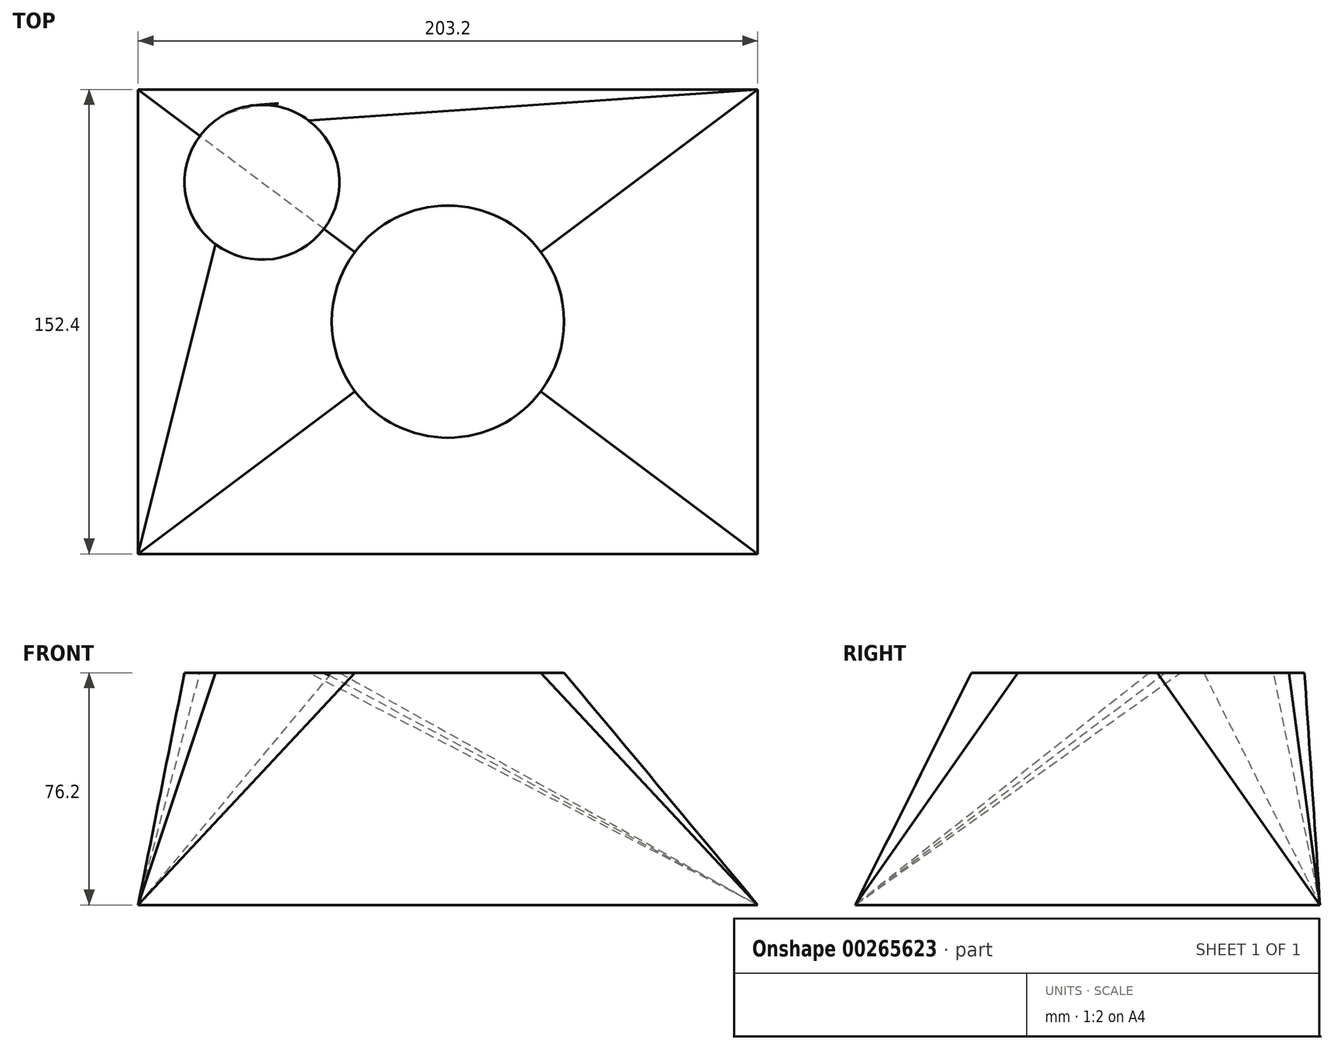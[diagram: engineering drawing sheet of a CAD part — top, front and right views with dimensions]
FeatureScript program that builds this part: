
annotation { "Feature Type Name" : "Feature", "Feature Type Description" : "" }
export const myFeature = defineFeature(function(context is Context, id is Id, definition is map)
    precondition{}
    {
        {
            var Q0;
            Q0=qCreatedBy(makeId("Top.planeOp"),FACE);
            cPlane(context, id + "F0", {"entities" : qUnion([Q0]), "cplaneType" : CPlaneType.OFFSET, "offset" : 76.2 * mm, "width" : 152.4 * mm, "height" : 152.4 * mm});
        }
        {
            var Q0;
            Q0=qCreatedBy(makeId("Top.planeOp"),FACE);
            var sketch = newSketch(context, id + "F1", { "sketchPlane" : qUnion([Q0])});
            skLineSegment(sketch, "E0.bottom", {"start": v(-101.6, 76.2) * mm, "end": v(101.6, 76.2) * mm});
            skLineSegment(sketch, "E0.top", {"start": v(-101.6, -76.2) * mm, "end": v(101.6, -76.2) * mm});
            skLineSegment(sketch, "E0.left", {"start": v(-101.6, 76.2) * mm, "end": v(-101.6, -76.2) * mm});
            skLineSegment(sketch, "E0.right", {"start": v(101.6, 76.2) * mm, "end": v(101.6, -76.2) * mm});
            skPoint(sketch, "E0.middle", {"position": v(0, 0) * mm});
            skSolve(sketch);
        }
        {
            var Q0;
            Q0=qCreatedBy(id+"F0.planeOp",FACE);
            var sketch = newSketch(context, id + "F2", { "sketchPlane" : qUnion([Q0])});
            skPoint(sketch, "E1.0", {"position": v(101.6, 76.2) * mm});
            skPoint(sketch, "E1.1", {"position": v(-101.6, 76.2) * mm});
            skPoint(sketch, "E1.2", {"position": v(101.6, -76.2) * mm});
            skPoint(sketch, "E1.3", {"position": v(-101.6, -76.2) * mm});
            skLineSegment(sketch, "E2", {"start": v(-101.6, 76.2) * mm, "end": v(-30.48, 22.86) * mm, "construction": true});
            skLineSegment(sketch, "E3", {"start": v(-101.6, -76.2) * mm, "end": v(30.48, 22.86) * mm, "construction": true});
            skLineSegment(sketch, "E4", {"start": v(-30.48, 22.86) * mm, "end": v(101.6, -76.2) * mm, "construction": true});
            skLineSegment(sketch, "E5", {"start": v(30.48, 22.86) * mm, "end": v(101.6, 76.2) * mm, "construction": true});
            skArc(sketch, "E6", {"start": v(30.48, -22.86) * mm, "mid": v(38.1, 0) * mm, "end": v(30.48, 22.86) * mm});
            skArc(sketch, "E7", {"start": v(-30.48, -22.86) * mm, "mid": v(0, -38.1) * mm, "end": v(30.48, -22.86) * mm});
            skLineSegment(sketch, "E8", {"start": v(30.48, 22.86) * mm, "end": v(30.48, 22.86) * mm});
            skArc(sketch, "E9", {"start": v(-30.48, 22.86) * mm, "mid": v(-38.1, 0) * mm, "end": v(-30.48, -22.86) * mm});
            skArc(sketch, "E10", {"start": v(30.48, 22.86) * mm, "mid": v(0, 38.1) * mm, "end": v(-30.48, 22.86) * mm});
            skCircle(sketch, "E11", {"center": v(-60.96, 45.72) * mm, "radius": 25.4 * mm});
            skSolve(sketch);
        }
        {
            var Q0;
            Q0=makeQuery(id+"F1.imprint","IMPRINT",FACE,{"disambiguationData":[TD([[makeQuery(id+"F1.imprint","IMPRINT",EDGE,{"derivedFrom":sQuery(id+"F1.wireOp",EDGE,"E0.bottom")}),-1.0]])]});
            var Q1;
            Q1=makeQuery(id+"F2.imprint","IMPRINT",FACE,{"disambiguationData":[TD([[makeQuery(id+"F2.imprint","IMPRINT",EDGE,{"derivedFrom":sQuery(id+"F2.wireOp",EDGE,"E11")}),1.0]])]});
            loft(context, id + "F3", {"sheetProfilesArray" : [{ "sheetProfileEntities" : qUnion([Q0]) }, { "sheetProfileEntities" : qUnion([Q1]) }]});
        }
        {
            var Q0;
            Q0=makeQuery(id+"F1.imprint","IMPRINT",FACE,{"disambiguationData":[TD([[makeQuery(id+"F1.imprint","IMPRINT",EDGE,{"derivedFrom":sQuery(id+"F1.wireOp",EDGE,"E0.bottom")}),-1.0]])]});
            var Q1;
            Q1=makeQuery(id+"F2.imprint","IMPRINT",FACE,{"disambiguationData":[TD([[makeQuery(id+"F2.imprint","IMPRINT",EDGE,{"derivedFrom":sQuery(id+"F2.wireOp",EDGE,"E6")}),1.0]])]});
            loft(context, id + "F4", {"sheetProfilesArray" : [{ "sheetProfileEntities" : qUnion([Q0]) }, { "sheetProfileEntities" : qUnion([Q1]) }]});
        }
    });
